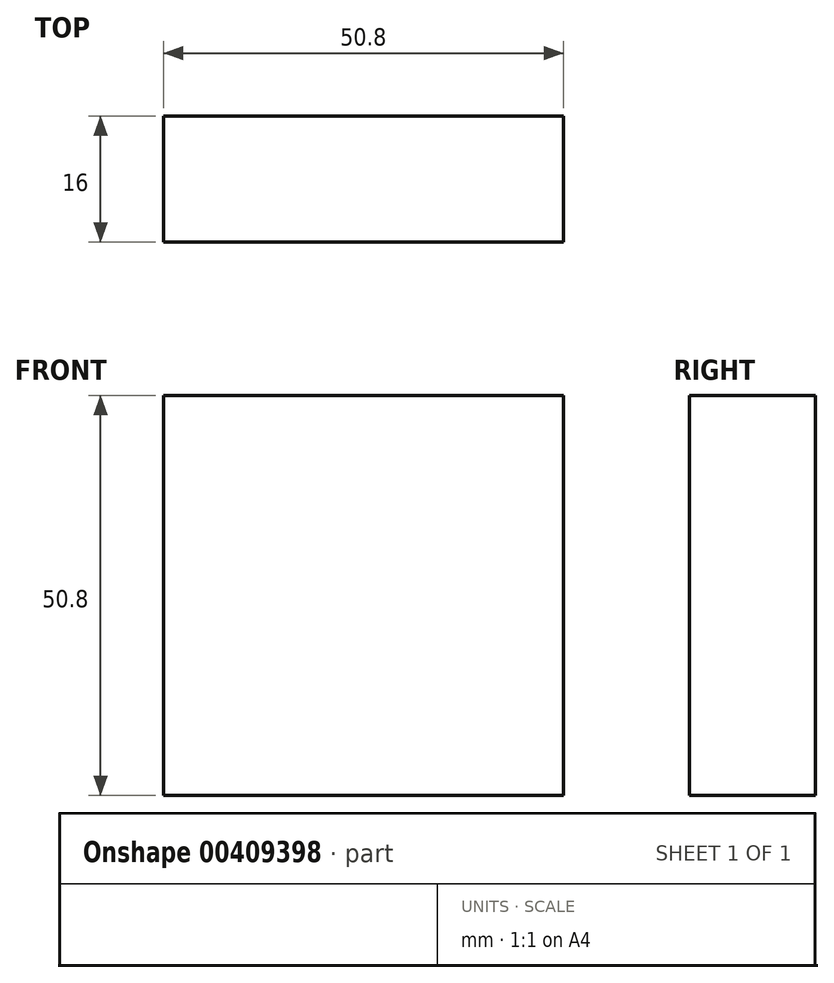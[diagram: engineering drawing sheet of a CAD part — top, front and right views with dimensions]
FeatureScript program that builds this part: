
annotation { "Feature Type Name" : "Feature", "Feature Type Description" : "" }
export const myFeature = defineFeature(function(context is Context, id is Id, definition is map)
    precondition{}
    {
        {
            var Q0;
            Q0=qCreatedBy(makeId("Front.planeOp"),FACE);
            var sketch = newSketch(context, id + "F0", { "sketchPlane" : qUnion([Q0])});
            skLineSegment(sketch, "E0.bottom", {"start": v(0, 0) * mm, "end": v(50.8, 0) * mm});
            skLineSegment(sketch, "E0.top", {"start": v(0, -50.8) * mm, "end": v(50.8, -50.8) * mm});
            skLineSegment(sketch, "E0.left", {"start": v(0, 0) * mm, "end": v(0, -50.8) * mm});
            skLineSegment(sketch, "E0.right", {"start": v(50.8, 0) * mm, "end": v(50.8, -50.8) * mm});
            skSolve(sketch);
        }
        {
            var Q0;
            Q0 = qSketchRegion(id + "F0", true);
            extrude(context, id + "F1", {"entities" : qUnion([Q0]), "depth" : 16 * mm});
        }
    });
